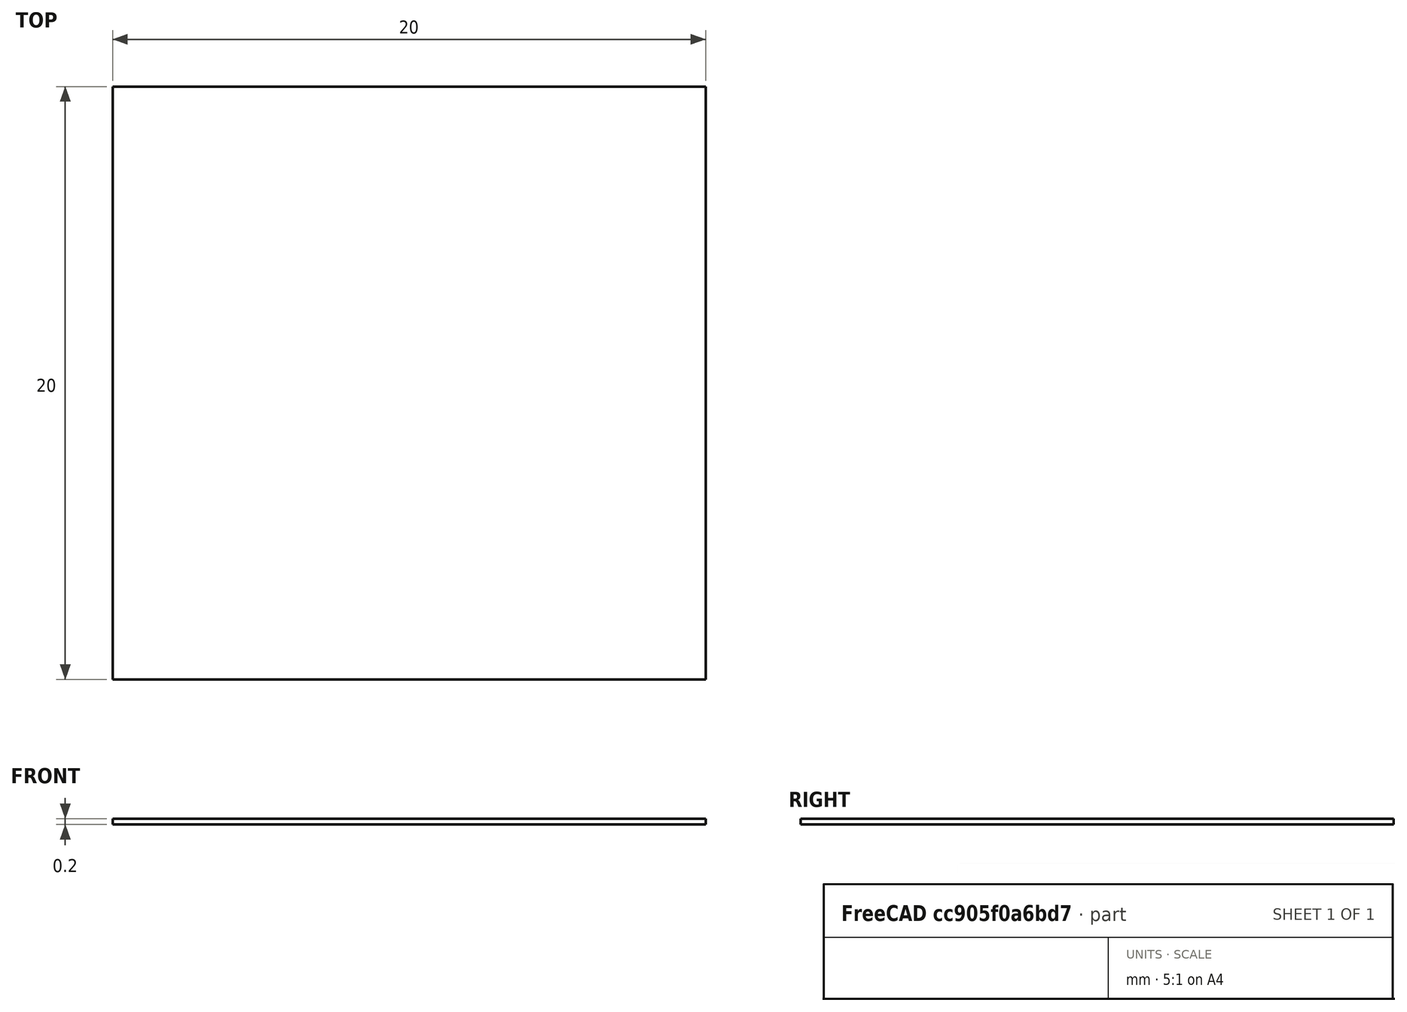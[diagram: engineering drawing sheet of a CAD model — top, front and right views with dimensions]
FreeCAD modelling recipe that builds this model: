
FCSTD DOCUMENT  (FreeCAD 0.18R4 (GitTag))
Label: TestFlatSquare
License: All rights reserved
LicenseURL: http://en.wikipedia.org/wiki/All_rights_reserved
objects: Sketcher::SketchObject×1, PartDesign::Pad×1, PartDesign::Body×1
note: 4 computed .brp shape members not serialized (recipe doc carries the construction recipe); baked Part::Feature solids carry a one-line shape summary decoded from their .brp

FEATURE [Sketcher::SketchObject] Sketch
  MapMode = 5
  Support = -> [XY_Plane]
  sketch-geometry (4):
    g0: LineSegment StartX=-10 StartY=10 StartZ=0 EndX=10 EndY=10 EndZ=0
    g1: LineSegment StartX=10 StartY=10 StartZ=0 EndX=10 EndY=-10 EndZ=0
    g2: LineSegment StartX=10 StartY=-10 StartZ=0 EndX=-10 EndY=-10 EndZ=0
    g3: LineSegment StartX=-10 StartY=-10 StartZ=0 EndX=-10 EndY=10 EndZ=0
  constraints (12):
    c: Coincident(g0,g1)
    c: Coincident(g1,g2)
    c: Coincident(g2,g3)
    c: Coincident(g3,g0)
    c: Horizontal(g0)
    c: Horizontal(g2)
    c: Vertical(g1)
    c: Vertical(g3)
    c: DistanceX(g0,g-1) = 10
    c: DistanceX(g0,g0) = 20
    c: DistanceY(g-1,g0) = 10
    c: DistanceY(g1,g0) = 20
FEATURE [PartDesign::Pad] Pad
  Length = 0.2
  Length2 = 100
  Profile = -> Sketch
  Type = 0
FEATURE [PartDesign::Body] Body  label="TestFlatSquare"
  Group = -> [Sketch,Pad]
  Origin = -> Origin
  Tip = -> Pad
